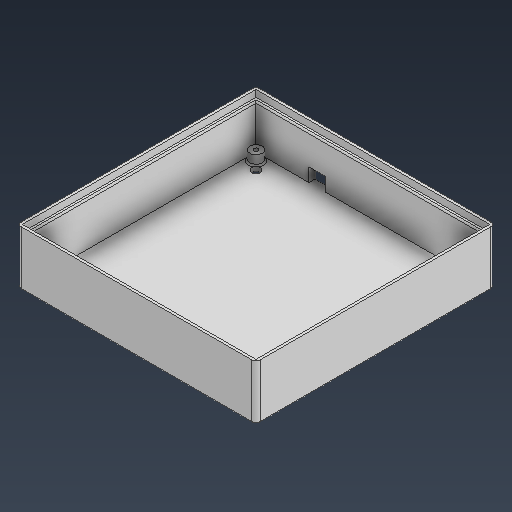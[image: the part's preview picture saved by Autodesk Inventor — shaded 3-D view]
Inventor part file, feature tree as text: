
AUTODESK INVENTOR PART (.ipt)
format: ipt  version: 2025.3 (Build 293356000, 356)  size: 273,920 bytes
history: native  units: mm
features: sketch x9, extrude x7, projected_geometry x5, fillet x4, hole x1
ambient origin geometry x8: Origin, YZ Plane, XZ Plane, XY Plane, X Axis, Y Axis, Z Axis, Center Point
bodies: Solid1 (feature_tree)
feature tree (26):
  extrude  "Extrusion1"  Depth=175.0mm
  extrude  "Extrusion2"  Depth=37.09mm TaperAngle=0.0deg
  extrude  "Extrusion3"  Depth=171.2mm
  extrude  "Extrusion5"  Depth=165.0mm
  hole  "Hole1"  [1 undecoded]
  extrude  "Extrusion7"  Depth=27.0mm
  extrude  "Extrusion8"  Depth=5.0mm
  extrude  "Extrusion9"  Depth=5.0mm
  fillet  "Fillet1"  Radius=7.0mm
  fillet  "Fillet2"  Radius=9.2mm
  fillet  "Fillet3"  Radius=9.2mm
  fillet  "Fillet4"  Radius=9.2mm
  sketch  "Sketch1"  dims[d0=175.0mm d1=175.0mm]
  sketch  "Sketch2"  dims[d8=5.0mm d9=0.0mm d20=171.2mm]
  projected_geometry  "Projected Loop1"
  sketch  "Sketch3"  dims[d21=166.0mm d22=165.0mm]
  projected_geometry  "Projected Loop2"
  sketch  "Sketch5"  dims[d23=5.0mm d27=5.0mm]
  projected_geometry  "Projected Loop4"
  sketch  "Sketch8"  dims[d34=8.0mm d35=27.0mm]
  sketch  "Sketch9"  dims[d36=5.0mm d37=5.0mm]
  projected_geometry  "Projected Loop5"
  sketch  "Sketch10"  dims[d38=5.0mm d39=5.0mm d40=7.0mm d41=0.0mm d45=9.2mm d46=9.2mm d47=9.2mm]
  sketch  "Sketch Rectangular Pattern1"  dims[d2=3.0mm d3=0.0mm d5=37.09mm d6=0.0mm]
  sketch  "Sketch11"  dims[d48=9.2mm d51=3.2mm d52=6.0mm d53=4.0mm d54=2.0mm d55=90.0deg d56=8.0mm d57=20.594885mm d58=44.765mm d59=12.0mm d60=10.0mm d61=1.6mm d62=10.0mm d63=0.0mm d64=6.4mm d65=16.0mm d66=16.0mm d67=20.0mm d69=143.0mm d70=20.0mm d72=143.0mm d75=10.0mm d76=0.0mm d77=6.0mm d78=6.0mm d79=6.0mm d80=6.0mm d81=4.0mm d82=0.0mm d83=3.0mm d84=1.0mm d85=1.1mm d86=1.0mm]
  projected_geometry  "Projected Loop6"
note: 1 required parameter value undecoded (feature->parameter linkage not recoverable at this tier; creation-order binding heuristic only, values carry confidence <= 0.55)
